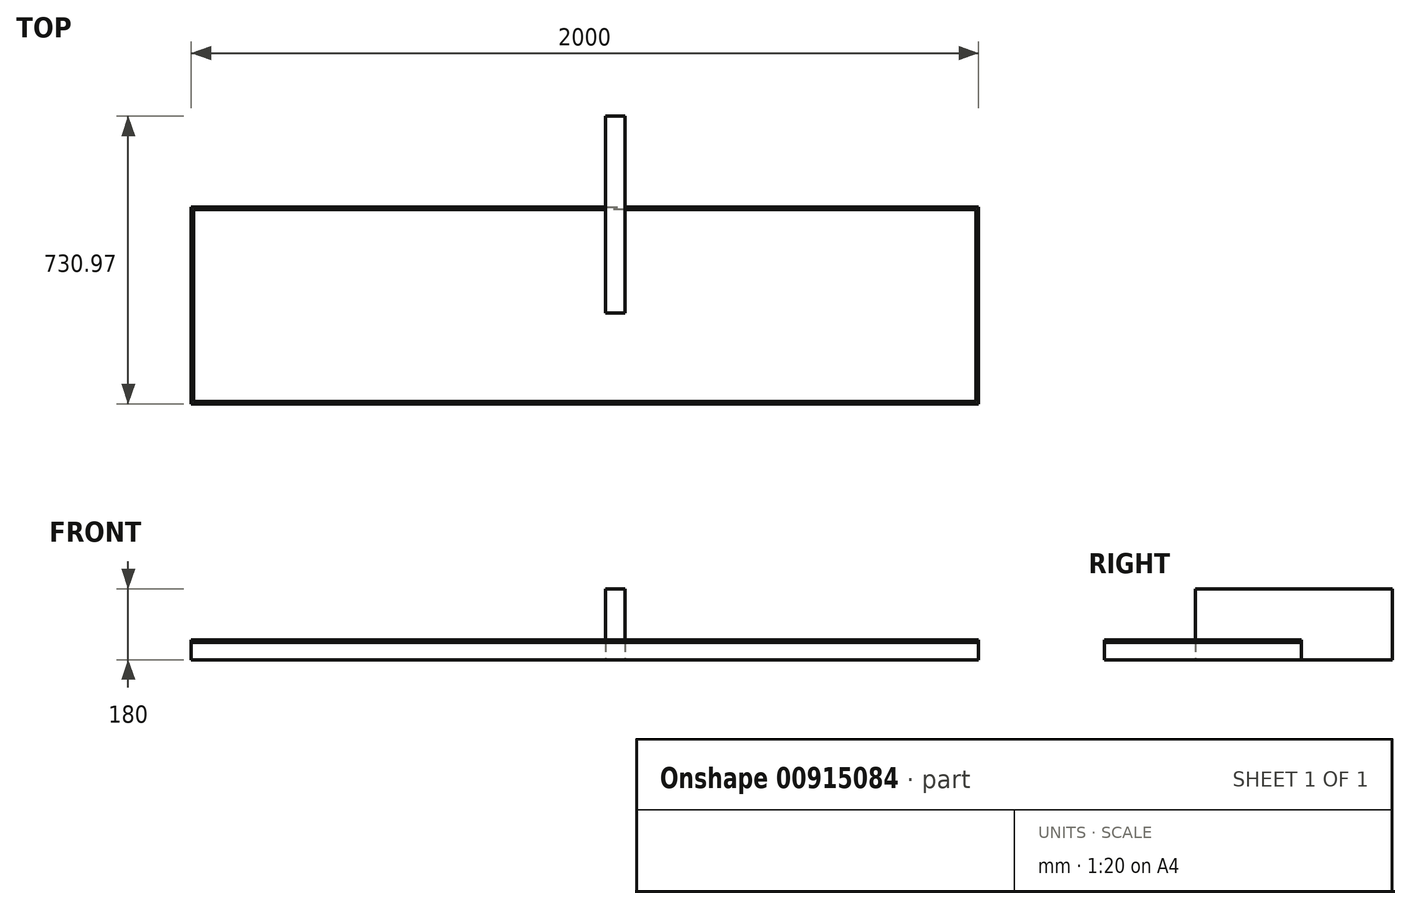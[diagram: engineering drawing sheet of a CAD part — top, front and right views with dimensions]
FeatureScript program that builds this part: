
annotation { "Feature Type Name" : "Feature", "Feature Type Description" : "" }
export const myFeature = defineFeature(function(context is Context, id is Id, definition is map)
    precondition{}
    {
        {
            var Q0;
            Q0=qCreatedBy(makeId("Top.planeOp"),FACE);
            var sketch = newSketch(context, id + "F0", { "sketchPlane" : qUnion([Q0])});
            skLineSegment(sketch, "E0.bottom", {"start": v(-991.14, 139.78) * mm, "end": v(1008.86, 139.78) * mm});
            skLineSegment(sketch, "E0.top", {"start": v(-991.14, -360.22) * mm, "end": v(1008.86, -360.22) * mm});
            skLineSegment(sketch, "E0.left", {"start": v(-991.14, 139.78) * mm, "end": v(-991.14, -360.22) * mm});
            skLineSegment(sketch, "E0.right", {"start": v(1008.86, 139.78) * mm, "end": v(1008.86, -360.22) * mm});
            skSolve(sketch);
        }
        {
            var Q0;
            Q0 = qSketchRegion(id + "F0", true);
            extrude(context, id + "F1", {"entities" : qUnion([Q0]), "depth" : 50 * mm, "offsetDistance" : 25 * mm});
        }
        {
            var Q0;
            Q0=qCreatedBy(makeId("Top.planeOp"),FACE);
            var sketch = newSketch(context, id + "F2", { "sketchPlane" : qUnion([Q0])});
            skLineSegment(sketch, "E1.bottom", {"start": v(61.25, 370.75) * mm, "end": v(111.25, 370.75) * mm});
            skLineSegment(sketch, "E1.top", {"start": v(61.25, -129.25) * mm, "end": v(111.25, -129.25) * mm});
            skLineSegment(sketch, "E1.left", {"start": v(61.25, 370.75) * mm, "end": v(61.25, -129.25) * mm});
            skLineSegment(sketch, "E1.right", {"start": v(111.25, 370.75) * mm, "end": v(111.25, -129.25) * mm});
            skSolve(sketch);
        }
        {
            var Q0;
            Q0 = qSketchRegion(id + "F2", true);
            extrude(context, id + "F3", {"entities" : qUnion([Q0]), "depth" : 180 * mm, "offsetDistance" : 25 * mm});
        }
        {
            var Q0;
            Q0=makeQuery(id+"F1.opExtrude","SWEPT_BODY",BODY,{"disambiguationData":[OSD([sQuery(id+"F0.wireOp",EDGE,"E0.bottom"),sQuery(id+"F0.wireOp",EDGE,"E0.top"),sQuery(id+"F0.wireOp",EDGE,"E0.left"),sQuery(id+"F0.wireOp",EDGE,"E0.right")])]});
            transform(context, id + "F4", {"entities" : qUnion([Q0]), "transformType" : TransformType.TRANSLATION_3D, "dx" : 0 * mm, "dy" : 0 * mm, "dz" : 0 * mm, "makeCopy" : true});
        }
        {
            var Q0;
            Q0=makeQuery(id+"F1.opExtrude","CAP_EDGE",EDGE,{"disambiguationData":[OSD([sQuery(id+"F0.wireOp",EDGE,"E0.top")])],"isStart":false});
            var Q1;
            Q1=makeQuery(id+"F1.opExtrude","CAP_EDGE",EDGE,{"disambiguationData":[OSD([sQuery(id+"F0.wireOp",EDGE,"E0.left")])],"isStart":false});
            var Q2;
            Q2=makeQuery(id+"F1.opExtrude","CAP_EDGE",EDGE,{"disambiguationData":[OSD([sQuery(id+"F0.wireOp",EDGE,"E0.bottom")])],"isStart":false});
            var Q3;
            Q3=makeQuery(id+"F1.opExtrude","CAP_EDGE",EDGE,{"disambiguationData":[OSD([sQuery(id+"F0.wireOp",EDGE,"E0.right")])],"isStart":false});
            chamfer(context, id + "F5", {"entities" : qUnion([Q0, Q1, Q2, Q3]), "width" : 6 * mm, "tangentPropagation" : true});
        }
    });
